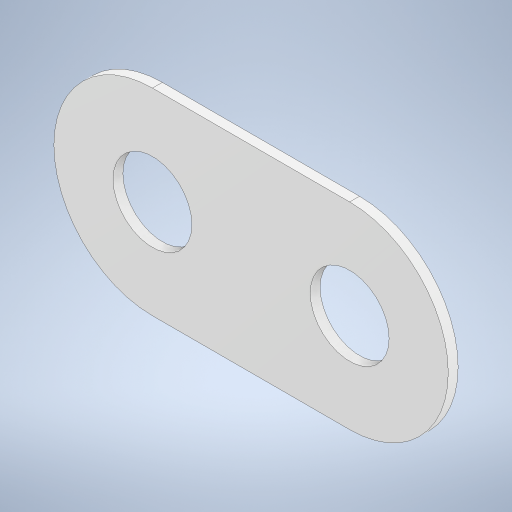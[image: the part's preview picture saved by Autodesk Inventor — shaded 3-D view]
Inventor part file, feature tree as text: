
AUTODESK INVENTOR PART (.ipt)
format: ipt  version: 2024 (Build 280153000, 153)  size: 251,904 bytes
history: native  units: mm
features: extrude x2, sketch x2, other x1, pattern_linear x1
ambient origin geometry x8: Origin, YZ Plane, XZ Plane, XY Plane, X Axis, Y Axis, Z Axis, Center Point
bodies: Body1 (feature_tree)
feature tree (6):
  other  "Těleso1"
  extrude  "Vysunutí1"  Depth=10.0mm
  extrude  "Vysunutí2"  Depth=5.0mm
  pattern_linear  "Obdélníkové pole1"  Spacing1=0.5mm  [1 undecoded]
  sketch  "Náčrt1"
  sketch  "Náčrt2"
note: 1 required parameter value undecoded (feature->parameter linkage not recoverable at this tier; creation-order binding heuristic only, values carry confidence <= 0.55)
